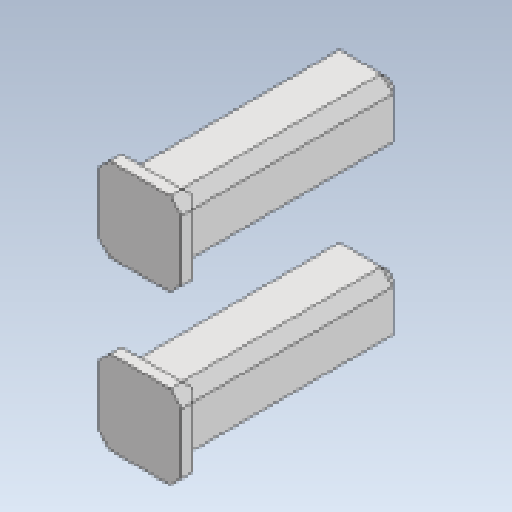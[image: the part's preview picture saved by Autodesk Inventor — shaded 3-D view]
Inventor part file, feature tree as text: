
AUTODESK INVENTOR PART (.ipt)
format: ipt  version: 2023 (Build 270158030, 158C)  size: 181,760 bytes
history: native  units: mm
features: other x5, chamfer x3, extrude x2, sketch x2, reference x2
ambient origin geometry x8: Origin, YZ Plane, XZ Plane, XY Plane, X Axis, Y Axis, Z Axis, Center Point
bodies: Body1 (feature_tree)
feature tree (14):
  other  "V4-pegs"
  extrude  "Extrusion1"  Depth=0.1mm
  extrude  "Extrusion3"  Depth=0.4mm TaperAngle=45.0deg
  chamfer  "Chamfer1"  Distance=0.5mm Angle=45.0deg
  chamfer  "Chamfer2"  Distance=6.0mm
  chamfer  "Chamfer3"  Distance=0.5mm
  sketch  "Sketch1"  dims[d0=0.1mm d1=0.1mm]
  reference  "Reference1"
  sketch  "Sketch3"  dims[d2=3.5mm d3=0.0mm d6=0.4mm d7=2.0mm d8=45.0deg d9=0.5mm d10=2.0mm d11=45.0deg d12=6.0mm d13=0.0mm d14=0.5mm d15=0.0mm d16=0.5mm d17=2.0mm d18=45.0deg]
  reference  "Reference10"
  other  "<userpath>\Documents\0004-inventor\3D-CAD-main\trebuchet\V4.2-trebuchet-assembled.iam"
  other  "V4.2-trebuchet-assembled.iam"
  other  "V4-baseplate:1"
  other  "v4-latch:1"
